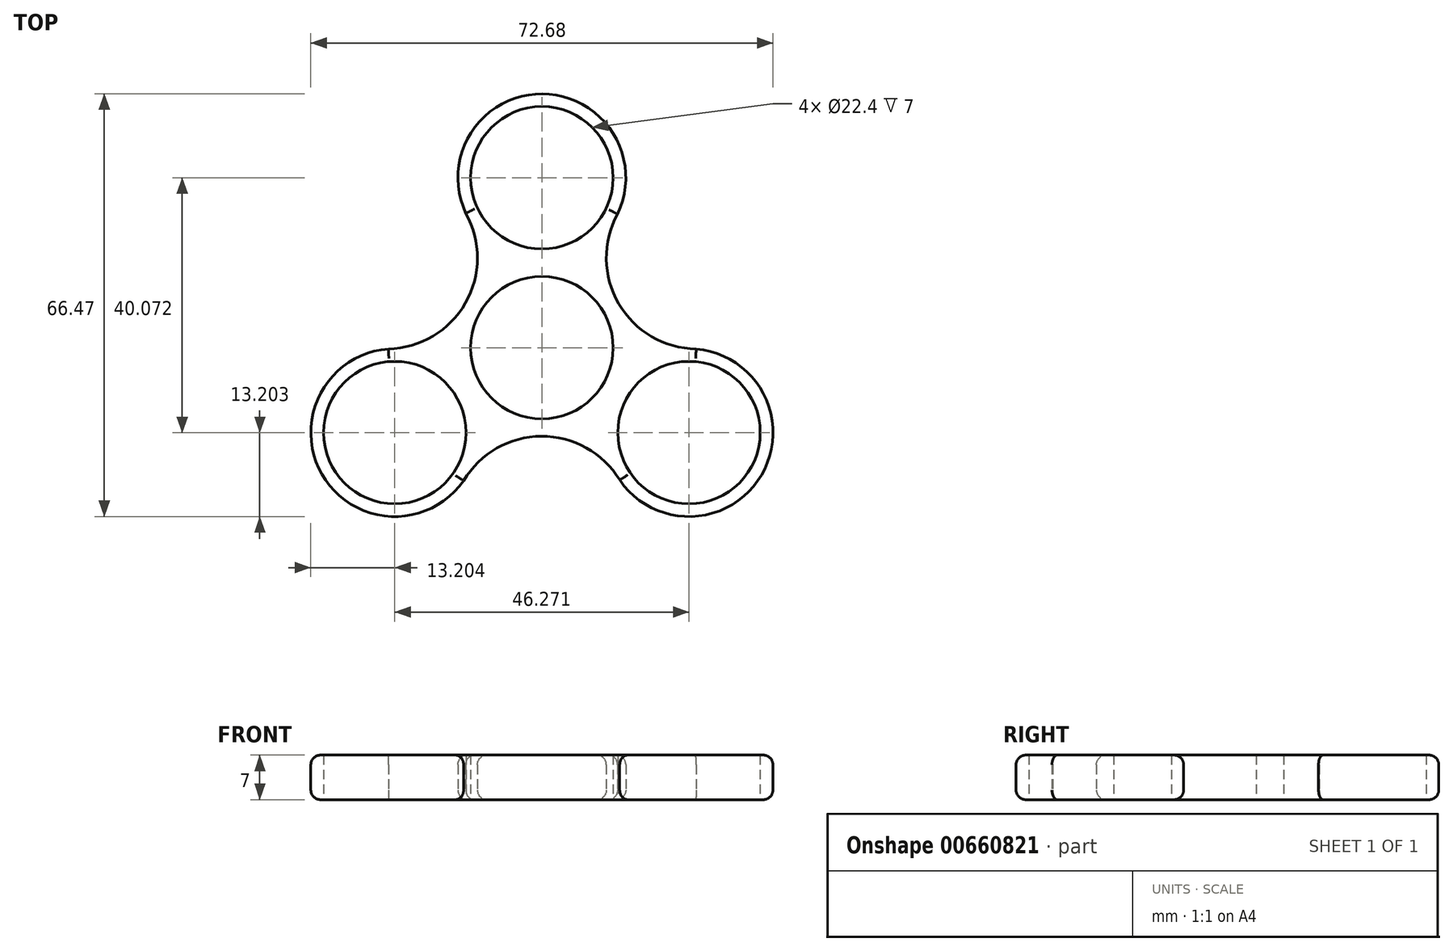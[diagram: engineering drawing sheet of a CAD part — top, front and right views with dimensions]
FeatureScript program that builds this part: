
annotation { "Feature Type Name" : "Feature", "Feature Type Description" : "" }
export const myFeature = defineFeature(function(context is Context, id is Id, definition is map)
    precondition{}
    {
        {
            var Q0;
            Q0=qCreatedBy(makeId("Top.planeOp"),FACE);
            var sketch = newSketch(context, id + "F0", { "sketchPlane" : qUnion([Q0])});
            skCircle(sketch, "E0", {"center": v(0, 0) * mm, "radius": 11.2 * mm});
            skCircle(sketch, "E1", {"center": v(0, 26.71) * mm, "radius": 11.2 * mm});
            skArc(sketch, "E2", {"start": v(11.56, 20.35) * mm, "mid": v(-0.06, 39.91) * mm, "end": v(-11.5, 20.24) * mm});
            skArc(sketch, "E3.1.0", {"start": v(-23.4, -0.16) * mm, "mid": v(-34.54, -20.01) * mm, "end": v(-11.78, -20.09) * mm});
            skCircle(sketch, "E3.1.1", {"center": v(-23.14, -13.36) * mm, "radius": 11.2 * mm});
            skArc(sketch, "E3.2.0", {"start": v(11.84, -20.2) * mm, "mid": v(34.6, -19.9) * mm, "end": v(23.28, -0.16) * mm});
            skCircle(sketch, "E3.2.1", {"center": v(23.14, -13.36) * mm, "radius": 11.2 * mm});
            skArc(sketch, "E4", {"start": v(11.9, 21) * mm, "mid": v(12.1, 6.9) * mm, "end": v(24.27, -0.2) * mm});
            skArc(sketch, "E5.1.0", {"start": v(-24.14, -0.2) * mm, "mid": v(-12.03, 7.02) * mm, "end": v(-11.96, 21.12) * mm});
            skArc(sketch, "E5.2.0", {"start": v(12.24, -20.8) * mm, "mid": v(-0.07, -13.92) * mm, "end": v(-12.31, -20.91) * mm});
            skSolve(sketch);
        }
        {
            var Q0;
            Q0=makeQuery(id+"F0.imprint","IMPRINT",FACE,{"disambiguationData":[TD([[makeQuery(id+"F0.imprint","IMPRINT",EDGE,{"derivedFrom":sQuery(id+"F0.wireOp",EDGE,"E0")}),-1.0]])]});
            extrude(context, id + "F1", {"entities" : qUnion([Q0]), "depth" : 7 * mm, "offsetDistance" : 25 * mm});
        }
        {
            var Q0;
            Q0=makeQuery(id+"F1.opExtrude","CAP_EDGE",EDGE,{"disambiguationData":[OSD([sQuery(id+"F0.wireOp",EDGE,"E3.1.0")])],"isStart":false});
            var Q1;
            Q1=makeQuery(id+"F1.opExtrude","CAP_EDGE",EDGE,{"disambiguationData":[OSD([sQuery(id+"F0.wireOp",EDGE,"E5.1.0")])],"isStart":false});
            var Q2;
            Q2=makeQuery(id+"F1.opExtrude","CAP_EDGE",EDGE,{"disambiguationData":[OSD([sQuery(id+"F0.wireOp",EDGE,"E4")])],"isStart":false});
            var Q3;
            Q3=makeQuery(id+"F1.opExtrude","CAP_EDGE",EDGE,{"disambiguationData":[OSD([sQuery(id+"F0.wireOp",EDGE,"E5.2.0")])],"isStart":false});
            var Q4;
            Q4=makeQuery(id+"F1.opExtrude","CAP_EDGE",EDGE,{"disambiguationData":[OSD([sQuery(id+"F0.wireOp",EDGE,"E3.2.0")])],"isStart":false});
            var Q5;
            Q5=makeQuery(id+"F1.opExtrude","CAP_EDGE",EDGE,{"disambiguationData":[OSD([sQuery(id+"F0.wireOp",EDGE,"E2")])],"isStart":false});
            fillet(context, id + "F2", {"entities" : qUnion([Q0, Q1, Q2, Q3, Q4, Q5]), "radius" : 1.5 * mm, "tangentPropagation" : true, "allowEdgeOverflow" : false});
        }
        {
            var Q0;
            Q0=makeQuery(id+"F1.opExtrude","CAP_EDGE",EDGE,{"disambiguationData":[OSD([sQuery(id+"F0.wireOp",EDGE,"E5.1.0")])],"isStart":true});
            var Q1;
            Q1=makeQuery(id+"F1.opExtrude","CAP_EDGE",EDGE,{"disambiguationData":[OSD([sQuery(id+"F0.wireOp",EDGE,"E3.1.0")])],"isStart":true});
            var Q2;
            Q2=makeQuery(id+"F1.opExtrude","CAP_EDGE",EDGE,{"disambiguationData":[OSD([sQuery(id+"F0.wireOp",EDGE,"E5.2.0")])],"isStart":true});
            var Q3;
            Q3=makeQuery(id+"F1.opExtrude","CAP_EDGE",EDGE,{"disambiguationData":[OSD([sQuery(id+"F0.wireOp",EDGE,"E3.2.0")])],"isStart":true});
            var Q4;
            Q4=makeQuery(id+"F1.opExtrude","CAP_EDGE",EDGE,{"disambiguationData":[OSD([sQuery(id+"F0.wireOp",EDGE,"E4")])],"isStart":true});
            var Q5;
            Q5=makeQuery(id+"F1.opExtrude","CAP_EDGE",EDGE,{"disambiguationData":[OSD([sQuery(id+"F0.wireOp",EDGE,"E2")])],"isStart":true});
            fillet(context, id + "F3", {"entities" : qUnion([Q0, Q1, Q2, Q3, Q4, Q5]), "radius" : 1.5 * mm, "tangentPropagation" : true, "allowEdgeOverflow" : false});
        }
    });
